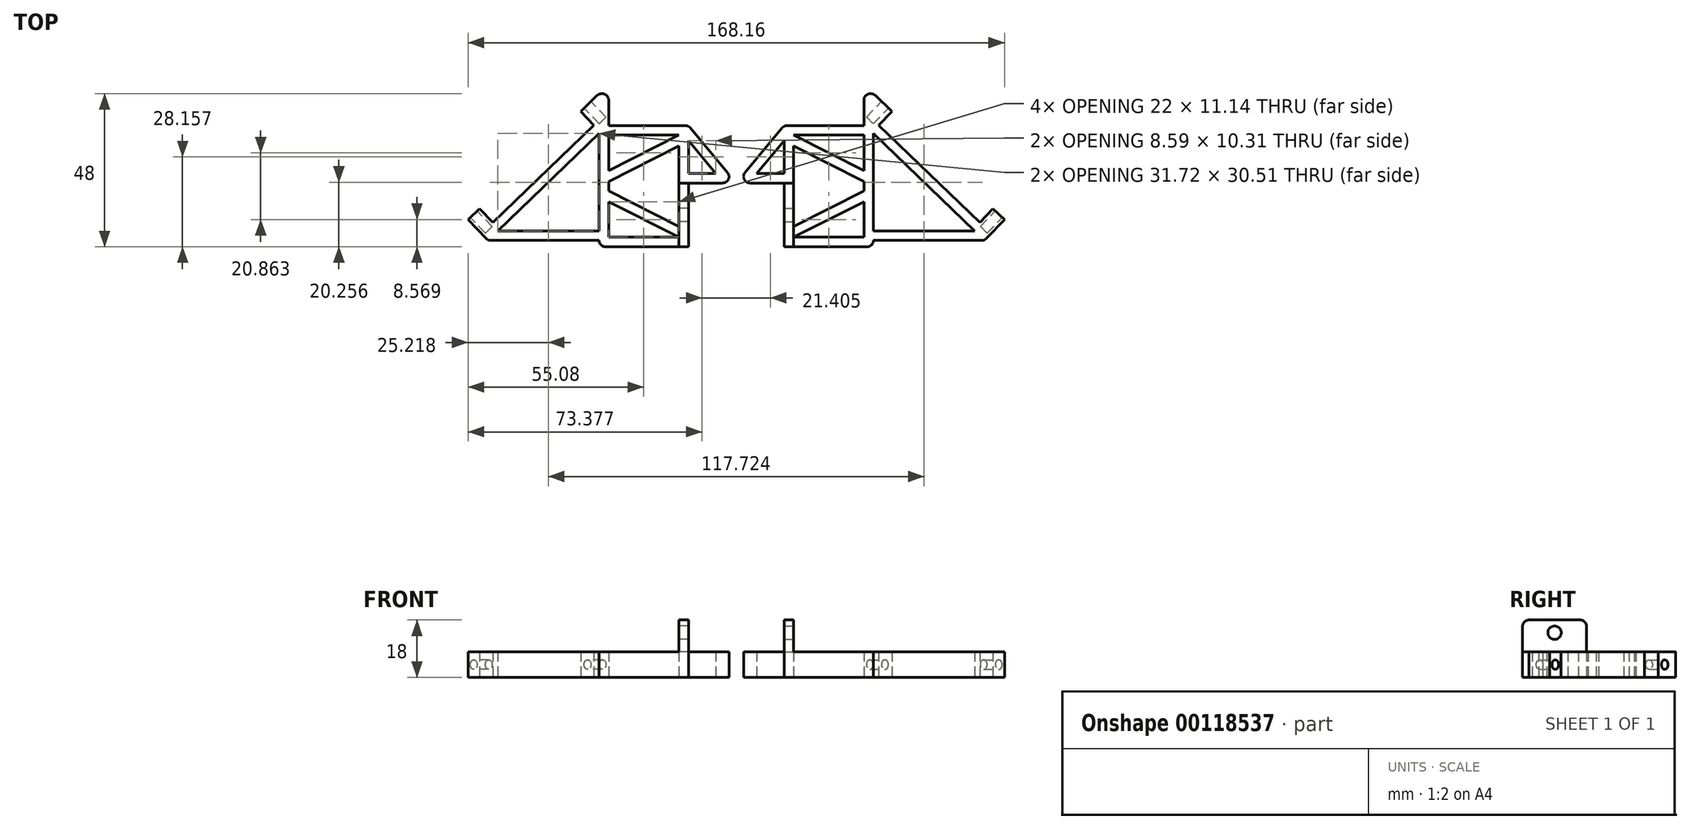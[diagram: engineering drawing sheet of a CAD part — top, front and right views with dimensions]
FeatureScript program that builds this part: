
annotation { "Feature Type Name" : "Feature", "Feature Type Description" : "" }
export const myFeature = defineFeature(function(context is Context, id is Id, definition is map)
    precondition{}
    {
        {
            var Q0;
            Q0=qCreatedBy(makeId("Top.planeOp"),FACE);
            var sketch = newSketch(context, id + "F0", { "sketchPlane" : qUnion([Q0])});
            skLineSegment(sketch, "E0", {"start": v(-43, 28) * mm, "end": v(-43, -20) * mm});
            skLineSegment(sketch, "E1", {"start": v(-43, -20) * mm, "end": v(-40, -20) * mm});
            skLineSegment(sketch, "E2", {"start": v(-40, -20) * mm, "end": v(-40, 28) * mm});
            skLineSegment(sketch, "E3", {"start": v(-40, 28) * mm, "end": v(-43, 28) * mm});
            skLineSegment(sketch, "E4", {"start": v(0, 0) * mm, "end": v(-15, 0) * mm});
            skLineSegment(sketch, "E5", {"start": v(-43, 19.68) * mm, "end": v(-79.92, -15.84) * mm});
            skLineSegment(sketch, "E6", {"start": v(-79.92, -15.84) * mm, "end": v(-77.84, -18) * mm});
            skLineSegment(sketch, "E7", {"start": v(-77.84, -18) * mm, "end": v(-43, 15.51) * mm});
            skLineSegment(sketch, "E8", {"start": v(-43, -15) * mm, "end": v(-74.72, -15) * mm});
            skLineSegment(sketch, "E9", {"start": v(-77.84, -18) * mm, "end": v(-43, -18) * mm});
            skLineSegment(sketch, "E10", {"start": v(-79.92, -15.84) * mm, "end": v(-84.08, -11.51) * mm});
            skLineSegment(sketch, "E11", {"start": v(-84.08, -11.51) * mm, "end": v(-80.48, -8.05) * mm});
            skLineSegment(sketch, "E12", {"start": v(-80.48, -8.05) * mm, "end": v(-76.32, -12.37) * mm});
            skLineSegment(sketch, "E13", {"start": v(-44.6, 18.13) * mm, "end": v(-48.77, 22.45) * mm});
            skLineSegment(sketch, "E14", {"start": v(-48.77, 22.45) * mm, "end": v(-43, 28) * mm});
            skLineSegment(sketch, "E15", {"start": v(0, 0) * mm, "end": v(-15, 18) * mm});
            skLineSegment(sketch, "E16", {"start": v(-15, 3) * mm, "end": v(-6.4, 3) * mm});
            skLineSegment(sketch, "E17", {"start": v(-6.4, 3) * mm, "end": v(-15, 13.31) * mm});
            skLineSegment(sketch, "E18", {"start": v(-15, 18) * mm, "end": v(-15, -20) * mm});
            skLineSegment(sketch, "E19", {"start": v(-15, -20) * mm, "end": v(-18, -20) * mm});
            skLineSegment(sketch, "E20", {"start": v(-18, -20) * mm, "end": v(-18, 18) * mm});
            skLineSegment(sketch, "E21", {"start": v(-18, 18) * mm, "end": v(-15, 18) * mm});
            skLineSegment(sketch, "E22", {"start": v(-18, 18) * mm, "end": v(-40, 18) * mm});
            skLineSegment(sketch, "E23", {"start": v(-18, 15) * mm, "end": v(-40, 15) * mm});
            skLineSegment(sketch, "E24", {"start": v(-40, -2.5) * mm, "end": v(-18, -2.5) * mm});
            skLineSegment(sketch, "E25", {"start": v(-18, 0.5) * mm, "end": v(-40, 0.5) * mm});
            skLineSegment(sketch, "E26", {"start": v(-40, 0.5) * mm, "end": v(-18, 11.64) * mm});
            skLineSegment(sketch, "E27", {"start": v(-18, 15) * mm, "end": v(-40, 3.86) * mm});
            skLineSegment(sketch, "E28", {"start": v(-18, -20) * mm, "end": v(-40, -20) * mm});
            skLineSegment(sketch, "E29", {"start": v(-18, -17) * mm, "end": v(-40, -17) * mm});
            skLineSegment(sketch, "E30", {"start": v(-40, -2.5) * mm, "end": v(-18, -13.64) * mm});
            skLineSegment(sketch, "E31", {"start": v(-18, -17) * mm, "end": v(-40, -5.86) * mm});
            skSolve(sketch);
        }
        {
            var Q0;
            Q0=qSketchRegion(id+"F0",true);
            var Q1;
            {var subQ0=sQuery(id+"F0.wireOp",EDGE,"E30");Q1=makeQuery(id+"F0.imprint","IMPRINT",FACE,{"disambiguationData":[TD([[makeQuery(id+"F0.imprint","IMPRINT",EDGE,{"derivedFrom":subQ0}),-1.0]])]});}
            var Q2;
            {var subQ0=sQuery(id+"F0.wireOp",EDGE,"E26");Q2=makeQuery(id+"F0.imprint","IMPRINT",FACE,{"disambiguationData":[TD([[makeQuery(id+"F0.imprint","IMPRINT",EDGE,{"derivedFrom":subQ0}),1.0]])]});}
            extrude(context, id + "F1", {"entities" : qUnion([Q0, Q1, Q2]), "depth" : 8 * mm});
        }
        {
            var Q0;
            Q0=makeQuery(id+"F1.opExtrude","SWEPT_FACE",FACE,{"disambiguationData":[OSD([sQuery(id+"F0.wireOp",EDGE,"E11")])]});
            var sketch = newSketch(context, id + "F2", { "sketchPlane" : qUnion([Q0])});
            skLineSegment(sketch, "E32", {"start": v(68.58, 4) * mm, "end": v(0, 4) * mm, "construction": true});
            skCircle(sketch, "E33", {"center": v(66.08, 4) * mm, "radius": 1.5 * mm});
            skCircle(sketch, "E34", {"center": v(16.58, 4) * mm, "radius": 1.5 * mm});
            skSolve(sketch);
        }
        {
            var Q0;
            Q0=qSketchRegion(id+"F2",true);
            extrude(context, id + "F3", {"entities" : qUnion([Q0]), "operationType" : NewBodyOperationType.REMOVE, "oppositeDirection" : true, "depth" : 6.8 * mm});
        }
        {
            var Q0;
            Q0=makeQuery(id+"F1.opExtrude","CAP_FACE",FACE,{"disambiguationData":[OSD([sQuery(id+"F0.wireOp",EDGE,"E0"),sQuery(id+"F0.wireOp",EDGE,"E1"),sQuery(id+"F0.wireOp",EDGE,"E2"),sQuery(id+"F0.wireOp",EDGE,"E3"),sQuery(id+"F0.wireOp",EDGE,"5tWljlZ9-UHUf-xyFz-PTxM-hxkn7qkuSnGL"),sQuery(id+"F0.wireOp",EDGE,"mZ4xgVsf-JCLs-Bvv0-jzmY-2kF2qlNNOxXa"),sQuery(id+"F0.wireOp",EDGE,"UeIPvYDs-Dcve-27Vh-hK3g-wKA9rX7bjYCd"),sQuery(id+"F0.wireOp",EDGE,"E4"),sQuery(id+"F0.wireOp",EDGE,"E5"),sQuery(id+"F0.wireOp",EDGE,"E6"),sQuery(id+"F0.wireOp",EDGE,"E7"),sQuery(id+"F0.wireOp",EDGE,"E8"),sQuery(id+"F0.wireOp",EDGE,"E9"),sQuery(id+"F0.wireOp",EDGE,"E10"),sQuery(id+"F0.wireOp",EDGE,"E11"),sQuery(id+"F0.wireOp",EDGE,"E12"),sQuery(id+"F0.wireOp",EDGE,"E13"),sQuery(id+"F0.wireOp",EDGE,"E14")])],"isStart":false});
            var sketch = newSketch(context, id + "F4", { "sketchPlane" : qUnion([Q0])});
            skLineSegment(sketch, "E35.0", {"start": v(-15, 0) * mm, "end": v(-15, -20) * mm});
            skLineSegment(sketch, "E36", {"start": v(-15, 0) * mm, "end": v(-18, 0) * mm});
            skLineSegment(sketch, "E37", {"start": v(-18, 0) * mm, "end": v(-18, -20) * mm});
            skLineSegment(sketch, "E38", {"start": v(-18, -20) * mm, "end": v(-15, -20) * mm});
            skSolve(sketch);
        }
        {
            var Q0;
            Q0=qSketchRegion(id+"F4",true);
            extrude(context, id + "F5", {"entities" : qUnion([Q0]), "operationType" : NewBodyOperationType.ADD, "depth" : 10 * mm});
        }
        {
            var Q0;
            Q0=makeQuery(id+"F1.opExtrude","SWEPT_EDGE",EDGE,{"disambiguationData":[OSD([sQuery(id+"F0.wireOp",EDGE,"E4"),sQuery(id+"F0.wireOp",EDGE,"E15")])]});
            var Q1;
            Q1=makeQuery(id+"F1.opExtrude","SWEPT_EDGE",EDGE,{"disambiguationData":[OSD([sQuery(id+"F0.wireOp",EDGE,"E0"),sQuery(id+"F0.wireOp",EDGE,"E1")])]});
            var Q2;
            Q2=makeQuery(id+"F1.opExtrude","SWEPT_EDGE",EDGE,{"disambiguationData":[OSD([sQuery(id+"F0.wireOp",EDGE,"E2"),sQuery(id+"F0.wireOp",EDGE,"E3")])]});
            var Q3;
            Q3=makeQuery(id+"F1.opExtrude","SWEPT_EDGE",EDGE,{"disambiguationData":[OSD([sQuery(id+"F0.wireOp",EDGE,"E0"),sQuery(id+"F0.wireOp",EDGE,"E3"),sQuery(id+"F0.wireOp",EDGE,"E14")])]});
            var Q4;
            Q4=makeQuery(id+"F1.opExtrude","SWEPT_EDGE",EDGE,{"disambiguationData":[OSD([sQuery(id+"F0.wireOp",EDGE,"E6"),sQuery(id+"F0.wireOp",EDGE,"E7"),sQuery(id+"F0.wireOp",EDGE,"E9")])]});
            var Q5;
            Q5=makeQuery(id+"F1.opExtrude","SWEPT_EDGE",EDGE,{"disambiguationData":[OSD([sQuery(id+"F0.wireOp",EDGE,"E15"),sQuery(id+"F0.wireOp",EDGE,"E18"),sQuery(id+"F0.wireOp",EDGE,"E21")])]});
            var Q6;
            Q6=makeQuery(id+"F5.opExtrude","CAP_EDGE",EDGE,{"disambiguationData":[OSD([sQuery(id+"F4.wireOp",EDGE,"E36")])],"isStart":false});
            var Q7;
            Q7=makeQuery(id+"F5.opExtrude","CAP_EDGE",EDGE,{"disambiguationData":[OSD([sQuery(id+"F4.wireOp",EDGE,"E38")])],"isStart":false});
            fillet(context, id + "F6", {"entities" : qUnion([Q0, Q1, Q2, Q3, Q4, Q5, Q6, Q7]), "radius" : 2 * mm, "tangentPropagation" : true, "allowEdgeOverflow" : false});
        }
        {
            var Q0;
            Q0=makeQuery(id+"F5.boolean.opBoolean","MERGE",FACE,{"derivedFrom":[makeQuery(id+"F1.opExtrude","SWEPT_FACE",FACE,{"disambiguationData":[OSD([sQuery(id+"F0.wireOp",EDGE,"E20")])]}),makeQuery(id+"F5.opExtrude","SWEPT_FACE",FACE,{"disambiguationData":[OSD([sQuery(id+"F4.wireOp",EDGE,"E37")])]})]});
            var sketch = newSketch(context, id + "F7", { "sketchPlane" : qUnion([Q0])});
            skLineSegment(sketch, "E39", {"start": v(10, 18) * mm, "end": v(10, 8) * mm, "construction": true});
            skCircle(sketch, "E40", {"center": v(10, 14) * mm, "radius": 2.1 * mm});
            skLineSegment(sketch, "E41", {"start": v(0, 8) * mm, "end": v(20, 8) * mm, "construction": true});
            skSolve(sketch);
        }
        {
            var Q0;
            Q0=qSketchRegion(id+"F7",true);
            extrude(context, id + "F8", {"entities" : qUnion([Q0]), "operationType" : NewBodyOperationType.REMOVE, "endBound" : BoundingType.THROUGH_ALL, "oppositeDirection" : true, "depth" : 25 * mm});
        }
        {
            var Q0;
            Q0=makeQuery(id+"F1.opExtrude","SWEPT_BODY",BODY,{"disambiguationData":[OSD([sQuery(id+"F0.wireOp",EDGE,"E0"),sQuery(id+"F0.wireOp",EDGE,"E1"),sQuery(id+"F0.wireOp",EDGE,"E2"),sQuery(id+"F0.wireOp",EDGE,"E3"),sQuery(id+"F0.wireOp",EDGE,"5tWljlZ9-UHUf-xyFz-PTxM-hxkn7qkuSnGL"),sQuery(id+"F0.wireOp",EDGE,"mZ4xgVsf-JCLs-Bvv0-jzmY-2kF2qlNNOxXa"),sQuery(id+"F0.wireOp",EDGE,"UeIPvYDs-Dcve-27Vh-hK3g-wKA9rX7bjYCd"),sQuery(id+"F0.wireOp",EDGE,"E4"),sQuery(id+"F0.wireOp",EDGE,"E5"),sQuery(id+"F0.wireOp",EDGE,"E6"),sQuery(id+"F0.wireOp",EDGE,"E7"),sQuery(id+"F0.wireOp",EDGE,"E8"),sQuery(id+"F0.wireOp",EDGE,"E9"),sQuery(id+"F0.wireOp",EDGE,"E10"),sQuery(id+"F0.wireOp",EDGE,"E11"),sQuery(id+"F0.wireOp",EDGE,"E12"),sQuery(id+"F0.wireOp",EDGE,"E13"),sQuery(id+"F0.wireOp",EDGE,"E14")])]});
            var Q1;
            Q1=qCreatedBy(makeId("Right.planeOp"),FACE);
            mirror(context, id + "F9", {"entities" : qUnion([Q0]), "mirrorPlane" : qUnion([Q1])});
        }
    });
